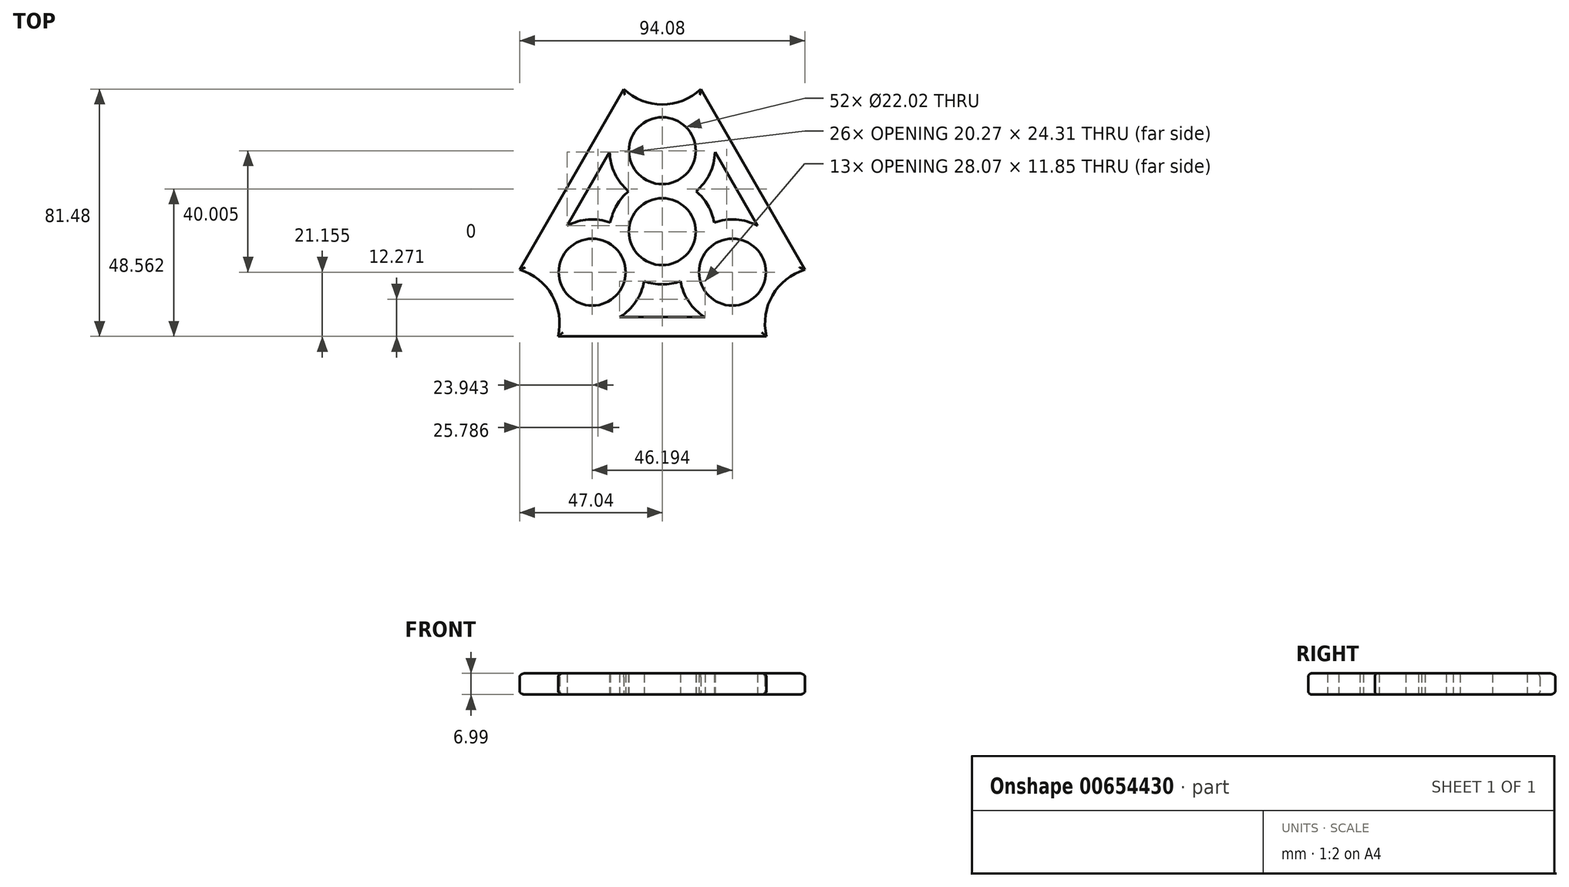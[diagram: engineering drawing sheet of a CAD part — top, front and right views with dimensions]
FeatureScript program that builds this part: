
annotation { "Feature Type Name" : "Feature", "Feature Type Description" : "" }
export const myFeature = defineFeature(function(context is Context, id is Id, definition is map)
    precondition{}
    {
        {
            var Q0;
            Q0=qCreatedBy(makeId("Top.planeOp"),FACE);
            var sketch = newSketch(context, id + "F0", { "sketchPlane" : qUnion([Q0])});
            skCircle(sketch, "E0", {"center": v(0, 0) * mm, "radius": 11.01 * mm});
            skCircle(sketch, "E1", {"center": v(0, 26.67) * mm, "radius": 11.01 * mm});
            skCircle(sketch, "E2", {"center": v(23.1, -13.33) * mm, "radius": 11.01 * mm});
            skCircle(sketch, "E3", {"center": v(-23.1, -13.33) * mm, "radius": 11.01 * mm});
            skLineSegment(sketch, "E4", {"start": v(0, 0) * mm, "end": v(-23.1, -13.33) * mm});
            skLineSegment(sketch, "E5", {"start": v(0, 0) * mm, "end": v(23.1, -13.34) * mm});
            skLineSegment(sketch, "E6", {"start": v(0, 0) * mm, "end": v(0, 26.67) * mm});
            skCircle(sketch, "E7", {"center": v(0, 0) * mm, "radius": 15.24 * mm});
            skCircle(sketch, "E8", {"center": v(23.1, -13.33) * mm, "radius": 15.24 * mm});
            skCircle(sketch, "E9", {"center": v(0, 26.67) * mm, "radius": 15.24 * mm});
            skCircle(sketch, "E10", {"center": v(-23.1, -13.33) * mm, "radius": 15.24 * mm});
            skLineSegment(sketch, "E11", {"start": v(-12.7, 46.99) * mm, "end": v(-47.04, -12.5) * mm});
            skLineSegment(sketch, "E12", {"start": v(-47.04, -12.5) * mm, "end": v(-34.34, -34.5) * mm});
            skLineSegment(sketch, "E13", {"start": v(-34.34, -34.5) * mm, "end": v(34.34, -34.5) * mm});
            skLineSegment(sketch, "E14", {"start": v(34.34, -34.5) * mm, "end": v(47.04, -12.5) * mm});
            skLineSegment(sketch, "E15", {"start": v(47.04, -12.5) * mm, "end": v(12.7, 46.99) * mm});
            skLineSegment(sketch, "E16", {"start": v(12.7, 46.99) * mm, "end": v(-12.7, 46.99) * mm});
            skLineSegment(sketch, "E17", {"start": v(0, 26.67) * mm, "end": v(0, 46.99) * mm});
            skLineSegment(sketch, "E18", {"start": v(-40.7, -23.5) * mm, "end": v(-23.1, -13.33) * mm});
            skLineSegment(sketch, "E19", {"start": v(40.7, -23.5) * mm, "end": v(23.1, -13.33) * mm});
            skArc(sketch, "E20", {"start": v(-12.7, 46.99) * mm, "mid": v(0, 41.91) * mm, "end": v(12.7, 46.99) * mm});
            skArc(sketch, "E21", {"start": v(-34.34, -34.5) * mm, "mid": v(-36.3, -20.96) * mm, "end": v(-47.04, -12.5) * mm});
            skArc(sketch, "E22", {"start": v(47.04, -12.5) * mm, "mid": v(36.3, -20.95) * mm, "end": v(34.34, -34.5) * mm});
            skSolve(sketch);
        }
        {
            var Q0;
            {var subQ0=sQuery(id+"F0.wireOp",EDGE,"E11");Q0=makeQuery(id+"F0.imprint","IMPRINT",FACE,{"disambiguationData":[TD([[makeQuery(id+"F0.imprint","IMPRINT",EDGE,{"derivedFrom":subQ0}),1.0]])]});}
            var Q1;
            {var subQ0=sQuery(id+"F0.wireOp",EDGE,"E13");Q1=makeQuery(id+"F0.imprint","IMPRINT",FACE,{"disambiguationData":[TD([[makeQuery(id+"F0.imprint","IMPRINT",EDGE,{"derivedFrom":subQ0}),1.0]])]});}
            var Q2;
            {var subQ5=sQuery(id+"F0.wireOp",EDGE,"E15");Q2=makeQuery(id+"F0.imprint","IMPRINT",FACE,{"disambiguationData":[TD([[makeQuery(id+"F0.imprint","IMPRINT",EDGE,{"derivedFrom":subQ5}),1.0]])]});}
            var Q3;
            {var subQ5=sQuery(id+"F0.wireOp",EDGE,"E6");var subQ6=sQuery(id+"F0.wireOp",EDGE,"E1");var subQ7=makeQuery(id+"F0.imprint","INTERSECT",VERTEX,{"derivedFrom":[subQ6,subQ5]});Q3=makeQuery(id+"F0.imprint","IMPRINT",FACE,{"disambiguationData":[TD([[makeQuery(id+"F0.imprint","IMPRINT",EDGE,{"disambiguationData":[TD([[subQ7,-1.0]])],"derivedFrom":subQ6}),-1.0]])]});}
            var Q4;
            {var subQ1=sQuery(id+"F0.wireOp",EDGE,"E6");var subQ5=sQuery(id+"F0.wireOp",EDGE,"E1");var subQ6=makeQuery(id+"F0.imprint","INTERSECT",VERTEX,{"derivedFrom":[subQ5,subQ1]});Q4=makeQuery(id+"F0.imprint","IMPRINT",FACE,{"disambiguationData":[TD([[makeQuery(id+"F0.imprint","IMPRINT",EDGE,{"disambiguationData":[TD([[subQ6,1.0]])],"derivedFrom":subQ5}),-1.0]])]});}
            var Q5;
            {var subQ6=sQuery(id+"F0.wireOp",EDGE,"E0");var subQ9=sQuery(id+"F0.wireOp",EDGE,"E4");var subQ11=makeQuery(id+"F0.imprint","INTERSECT",VERTEX,{"derivedFrom":[subQ6,subQ9]});Q5=makeQuery(id+"F0.imprint","IMPRINT",FACE,{"disambiguationData":[TD([[makeQuery(id+"F0.imprint","IMPRINT",EDGE,{"disambiguationData":[TD([[subQ11,1.0]])],"derivedFrom":subQ6}),-1.0]])]});}
            var Q6;
            {var subQ6=sQuery(id+"F0.wireOp",EDGE,"E0");var subQ9=sQuery(id+"F0.wireOp",EDGE,"E4");var subQ10=makeQuery(id+"F0.imprint","INTERSECT",VERTEX,{"derivedFrom":[subQ6,subQ9]});Q6=makeQuery(id+"F0.imprint","IMPRINT",FACE,{"disambiguationData":[TD([[makeQuery(id+"F0.imprint","IMPRINT",EDGE,{"disambiguationData":[TD([[subQ10,-1.0]])],"derivedFrom":subQ6}),-1.0]])]});}
            var Q7;
            {var subQ0=sQuery(id+"F0.wireOp",EDGE,"E6");var subQ1=sQuery(id+"F0.wireOp",EDGE,"E0");var subQ2=makeQuery(id+"F0.imprint","INTERSECT",VERTEX,{"derivedFrom":[subQ1,subQ0]});Q7=makeQuery(id+"F0.imprint","IMPRINT",FACE,{"disambiguationData":[TD([[makeQuery(id+"F0.imprint","IMPRINT",EDGE,{"disambiguationData":[TD([[subQ2,1.0]])],"derivedFrom":subQ1}),-1.0]])]});}
            var Q8;
            {var subQ0=sQuery(id+"F0.wireOp",EDGE,"E5");var subQ1=sQuery(id+"F0.wireOp",EDGE,"E2");var subQ2=makeQuery(id+"F0.imprint","INTERSECT",VERTEX,{"derivedFrom":[subQ1,subQ0]});Q8=makeQuery(id+"F0.imprint","IMPRINT",FACE,{"disambiguationData":[TD([[makeQuery(id+"F0.imprint","IMPRINT",EDGE,{"disambiguationData":[TD([[subQ2,-1.0]])],"derivedFrom":subQ1}),-1.0]])]});}
            var Q9;
            {var subQ0=sQuery(id+"F0.wireOp",EDGE,"E8");var subQ1=sQuery(id+"F0.wireOp",EDGE,"E5");var subQ2=makeQuery(id+"F0.imprint","INTERSECT",VERTEX,{"derivedFrom":[subQ1,subQ0]});Q9=makeQuery(id+"F0.imprint","IMPRINT",FACE,{"disambiguationData":[TD([[makeQuery(id+"F0.imprint","IMPRINT",EDGE,{"disambiguationData":[TD([[subQ2,-1.0]])],"derivedFrom":subQ1}),-1.0]])]});}
            var Q10;
            {var subQ0=sQuery(id+"F0.wireOp",EDGE,"E8");var subQ1=sQuery(id+"F0.wireOp",EDGE,"E5");var subQ2=makeQuery(id+"F0.imprint","INTERSECT",VERTEX,{"derivedFrom":[subQ1,subQ0]});Q10=makeQuery(id+"F0.imprint","IMPRINT",FACE,{"disambiguationData":[TD([[makeQuery(id+"F0.imprint","IMPRINT",EDGE,{"disambiguationData":[TD([[subQ2,-1.0]])],"derivedFrom":subQ1}),1.0]])]});}
            var Q11;
            {var subQ0=sQuery(id+"F0.wireOp",EDGE,"E5");var subQ1=sQuery(id+"F0.wireOp",EDGE,"E2");var subQ2=makeQuery(id+"F0.imprint","INTERSECT",VERTEX,{"derivedFrom":[subQ1,subQ0]});Q11=makeQuery(id+"F0.imprint","IMPRINT",FACE,{"disambiguationData":[TD([[makeQuery(id+"F0.imprint","IMPRINT",EDGE,{"disambiguationData":[TD([[subQ2,1.0]])],"derivedFrom":subQ1}),-1.0]])]});}
            var Q12;
            {var subQ5=sQuery(id+"F0.wireOp",EDGE,"E4");var subQ6=sQuery(id+"F0.wireOp",EDGE,"E3");var subQ7=makeQuery(id+"F0.imprint","INTERSECT",VERTEX,{"derivedFrom":[subQ6,subQ5]});Q12=makeQuery(id+"F0.imprint","IMPRINT",FACE,{"disambiguationData":[TD([[makeQuery(id+"F0.imprint","IMPRINT",EDGE,{"disambiguationData":[TD([[subQ7,1.0]])],"derivedFrom":subQ6}),-1.0]])]});}
            var Q13;
            {var subQ0=sQuery(id+"F0.wireOp",EDGE,"E10");var subQ1=sQuery(id+"F0.wireOp",EDGE,"E4");var subQ2=makeQuery(id+"F0.imprint","INTERSECT",VERTEX,{"derivedFrom":[subQ1,subQ0]});Q13=makeQuery(id+"F0.imprint","IMPRINT",FACE,{"disambiguationData":[TD([[makeQuery(id+"F0.imprint","IMPRINT",EDGE,{"disambiguationData":[TD([[subQ2,-1.0]])],"derivedFrom":subQ1}),1.0]])]});}
            var Q14;
            {var subQ0=sQuery(id+"F0.wireOp",EDGE,"E10");var subQ1=sQuery(id+"F0.wireOp",EDGE,"E4");var subQ2=makeQuery(id+"F0.imprint","INTERSECT",VERTEX,{"derivedFrom":[subQ1,subQ0]});Q14=makeQuery(id+"F0.imprint","IMPRINT",FACE,{"disambiguationData":[TD([[makeQuery(id+"F0.imprint","IMPRINT",EDGE,{"disambiguationData":[TD([[subQ2,-1.0]])],"derivedFrom":subQ1}),-1.0]])]});}
            var Q15;
            {var subQ0=sQuery(id+"F0.wireOp",EDGE,"E9");var subQ1=sQuery(id+"F0.wireOp",EDGE,"E6");var subQ2=makeQuery(id+"F0.imprint","INTERSECT",VERTEX,{"derivedFrom":[subQ1,subQ0]});Q15=makeQuery(id+"F0.imprint","IMPRINT",FACE,{"disambiguationData":[TD([[makeQuery(id+"F0.imprint","IMPRINT",EDGE,{"disambiguationData":[TD([[subQ2,-1.0]])],"derivedFrom":subQ1}),-1.0]])]});}
            var Q16;
            {var subQ0=sQuery(id+"F0.wireOp",EDGE,"E9");var subQ1=sQuery(id+"F0.wireOp",EDGE,"E6");var subQ2=makeQuery(id+"F0.imprint","INTERSECT",VERTEX,{"derivedFrom":[subQ1,subQ0]});Q16=makeQuery(id+"F0.imprint","IMPRINT",FACE,{"disambiguationData":[TD([[makeQuery(id+"F0.imprint","IMPRINT",EDGE,{"disambiguationData":[TD([[subQ2,-1.0]])],"derivedFrom":subQ1}),1.0]])]});}
            var Q17;
            {var subQ5=sQuery(id+"F0.wireOp",EDGE,"E4");var subQ7=sQuery(id+"F0.wireOp",EDGE,"E3");var subQ8=makeQuery(id+"F0.imprint","INTERSECT",VERTEX,{"derivedFrom":[subQ7,subQ5]});Q17=makeQuery(id+"F0.imprint","IMPRINT",FACE,{"disambiguationData":[TD([[makeQuery(id+"F0.imprint","IMPRINT",EDGE,{"disambiguationData":[TD([[subQ8,-1.0]])],"derivedFrom":subQ7}),-1.0]])]});}
            extrude(context, id + "F1", {"entities" : qUnion([Q0, Q1, Q2, Q3, Q4, Q5, Q6, Q7, Q8, Q9, Q10, Q11, Q12, Q13, Q14, Q15, Q16, Q17]), "depth" : 7 * mm, "offsetDistance" : 25.4 * mm});
        }
        {
            var Q0;
            Q0=makeQuery(id+"F1.opExtrude","CAP_FACE",FACE,{"disambiguationData":[OSD([sQuery(id+"F0.wireOp",EDGE,"E0"),sQuery(id+"F0.wireOp",EDGE,"E1"),sQuery(id+"F0.wireOp",EDGE,"E2"),sQuery(id+"F0.wireOp",EDGE,"E3"),sQuery(id+"F0.wireOp",EDGE,"E11"),sQuery(id+"F0.wireOp",EDGE,"E13"),sQuery(id+"F0.wireOp",EDGE,"E15"),sQuery(id+"F0.wireOp",EDGE,"E20"),sQuery(id+"F0.wireOp",EDGE,"E21"),sQuery(id+"F0.wireOp",EDGE,"E22")])],"isStart":false});
            var Q1;
            Q1=makeQuery(id+"F1.opExtrude","CAP_FACE",FACE,{"disambiguationData":[OSD([sQuery(id+"F0.wireOp",EDGE,"E0"),sQuery(id+"F0.wireOp",EDGE,"E1"),sQuery(id+"F0.wireOp",EDGE,"E2"),sQuery(id+"F0.wireOp",EDGE,"E3"),sQuery(id+"F0.wireOp",EDGE,"E11"),sQuery(id+"F0.wireOp",EDGE,"E13"),sQuery(id+"F0.wireOp",EDGE,"E15"),sQuery(id+"F0.wireOp",EDGE,"E20"),sQuery(id+"F0.wireOp",EDGE,"E21"),sQuery(id+"F0.wireOp",EDGE,"E22")])],"isStart":true});
            shell(context, id + "F2", {"entities" : qUnion([Q0, Q1]), "thickness" : 6.35 * mm});
        }
        {
            var Q0;
            Q0=makeQuery(id+"F1.opExtrude","CAP_EDGE",EDGE,{"disambiguationData":[OSD([sQuery(id+"F0.wireOp",EDGE,"E11")])],"isStart":false});
            var Q1;
            Q1=makeQuery(id+"F1.opExtrude","CAP_EDGE",EDGE,{"disambiguationData":[OSD([sQuery(id+"F0.wireOp",EDGE,"E20")])],"isStart":false});
            var Q2;
            Q2=makeQuery(id+"F1.opExtrude","CAP_EDGE",EDGE,{"disambiguationData":[OSD([sQuery(id+"F0.wireOp",EDGE,"E15")])],"isStart":false});
            var Q3;
            Q3=makeQuery(id+"F1.opExtrude","CAP_EDGE",EDGE,{"disambiguationData":[OSD([sQuery(id+"F0.wireOp",EDGE,"E22")])],"isStart":false});
            var Q4;
            Q4=makeQuery(id+"F1.opExtrude","CAP_EDGE",EDGE,{"disambiguationData":[OSD([sQuery(id+"F0.wireOp",EDGE,"E13")])],"isStart":false});
            var Q5;
            Q5=makeQuery(id+"F1.opExtrude","CAP_EDGE",EDGE,{"disambiguationData":[OSD([sQuery(id+"F0.wireOp",EDGE,"E21")])],"isStart":false});
            fillet(context, id + "F3", {"entities" : qUnion([Q0, Q1, Q2, Q3, Q4, Q5]), "radius" : 1.27 * mm, "tangentPropagation" : true, "allowEdgeOverflow" : false});
        }
        {
            var Q0;
            Q0=makeQuery(id+"F1.opExtrude","CAP_EDGE",EDGE,{"disambiguationData":[OSD([sQuery(id+"F0.wireOp",EDGE,"E15")])],"isStart":true});
            var Q1;
            Q1=makeQuery(id+"F1.opExtrude","CAP_EDGE",EDGE,{"disambiguationData":[OSD([sQuery(id+"F0.wireOp",EDGE,"E22")])],"isStart":true});
            var Q2;
            Q2=makeQuery(id+"F1.opExtrude","CAP_EDGE",EDGE,{"disambiguationData":[OSD([sQuery(id+"F0.wireOp",EDGE,"E13")])],"isStart":true});
            var Q3;
            Q3=makeQuery(id+"F1.opExtrude","CAP_EDGE",EDGE,{"disambiguationData":[OSD([sQuery(id+"F0.wireOp",EDGE,"E21")])],"isStart":true});
            var Q4;
            Q4=makeQuery(id+"F1.opExtrude","CAP_EDGE",EDGE,{"disambiguationData":[OSD([sQuery(id+"F0.wireOp",EDGE,"E11")])],"isStart":true});
            var Q5;
            Q5=makeQuery(id+"F1.opExtrude","CAP_EDGE",EDGE,{"disambiguationData":[OSD([sQuery(id+"F0.wireOp",EDGE,"E20")])],"isStart":true});
            fillet(context, id + "F4", {"entities" : qUnion([Q0, Q1, Q2, Q3, Q4, Q5]), "radius" : 1.27 * mm, "tangentPropagation" : true, "allowEdgeOverflow" : false});
        }
    });
